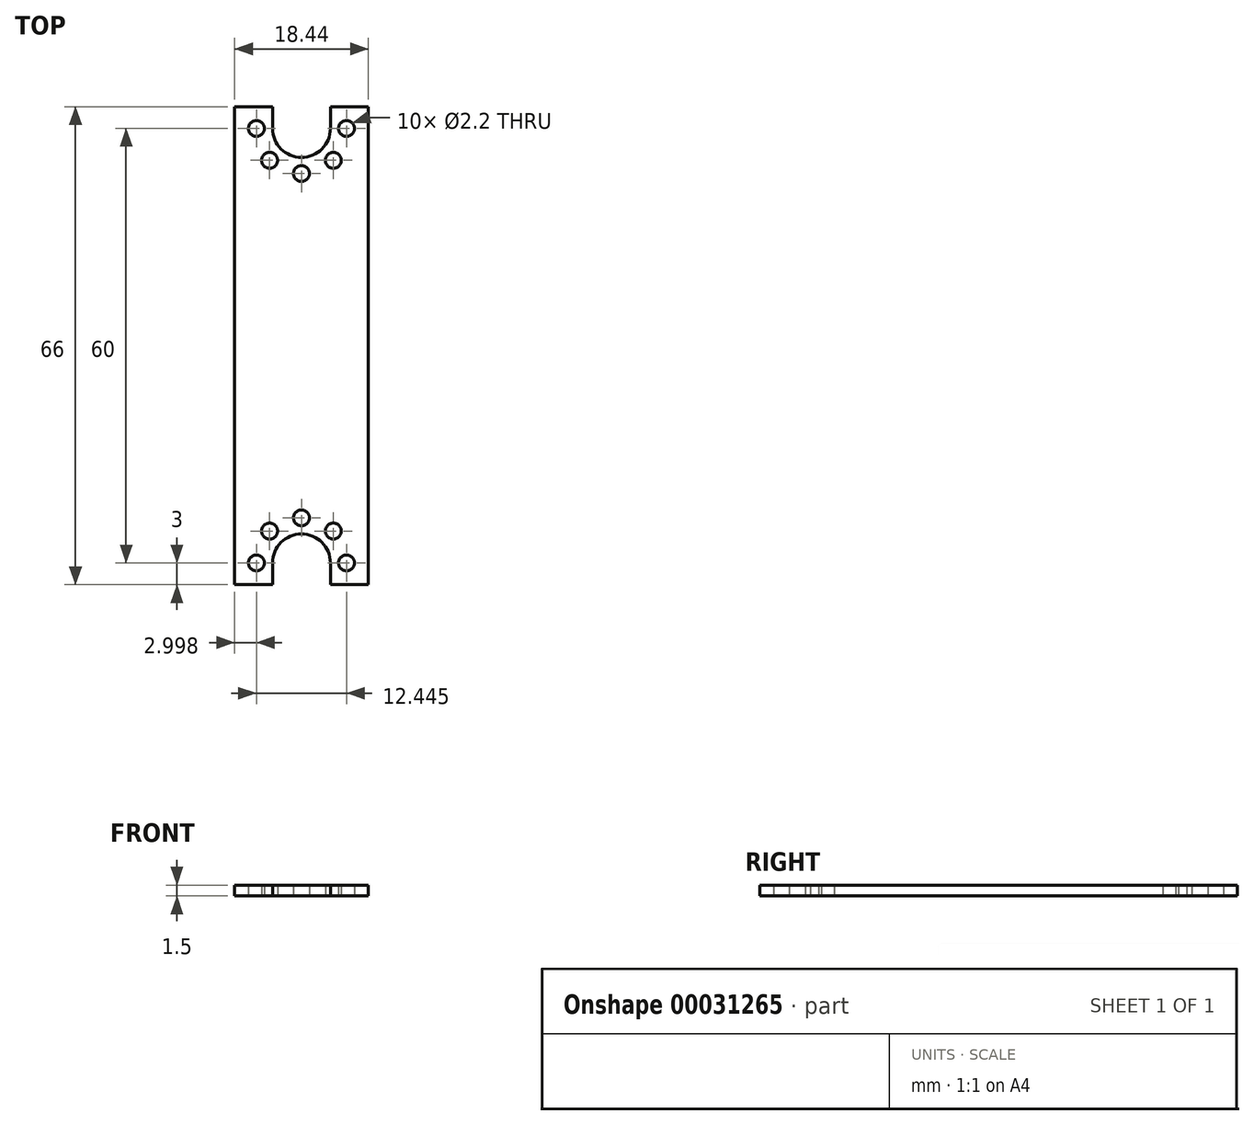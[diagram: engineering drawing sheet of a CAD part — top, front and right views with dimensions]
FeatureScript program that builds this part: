
annotation { "Feature Type Name" : "Feature", "Feature Type Description" : "" }
export const myFeature = defineFeature(function(context is Context, id is Id, definition is map)
    precondition{}
    {
        {
            var Q0;
            Q0=qCreatedBy(makeId("Top.planeOp"),FACE);
            var sketch = newSketch(context, id + "F0", { "sketchPlane" : qUnion([Q0])});
            skLineSegment(sketch, "E0.bottom", {"start": v(-9.22, 33) * mm, "end": v(9.22, 33) * mm});
            skLineSegment(sketch, "E0.top", {"start": v(-9.22, -33) * mm, "end": v(-4, -33) * mm});
            skLineSegment(sketch, "E0.left", {"start": v(-9.22, 33) * mm, "end": v(-9.22, -33) * mm});
            skLineSegment(sketch, "E0.right", {"start": v(9.22, 33) * mm, "end": v(9.22, 27.78) * mm});
            skPoint(sketch, "E0.middle", {"position": v(0, 0) * mm});
            skArc(sketch, "E1", {"start": v(6.22, 27.78) * mm, "mid": v(2.22, 23.78) * mm, "end": v(6.22, 19.78) * mm});
            skArc(sketch, "E2", {"start": v(4, -30) * mm, "mid": v(0, -26) * mm, "end": v(-4, -30) * mm});
            skLineSegment(sketch, "E3.bottom", {"start": v(1.82, 28.18) * mm, "end": v(10.62, 28.18) * mm, "construction": true});
            skLineSegment(sketch, "E3.top", {"start": v(1.82, 19.38) * mm, "end": v(10.62, 19.38) * mm, "construction": true});
            skLineSegment(sketch, "E3.left", {"start": v(1.82, 28.18) * mm, "end": v(1.82, 19.38) * mm, "construction": true});
            skLineSegment(sketch, "E3.right", {"start": v(10.62, 28.18) * mm, "end": v(10.62, 19.38) * mm, "construction": true});
            skCircle(sketch, "E4", {"center": v(1.82, 28.18) * mm, "radius": 1.1 * mm});
            skCircle(sketch, "E5.1.0", {"center": v(0, 23.78) * mm, "radius": 1.1 * mm});
            skCircle(sketch, "E5.2.0", {"center": v(1.82, 19.38) * mm, "radius": 1.1 * mm});
            skCircle(sketch, "E5.3.0", {"center": v(6.22, 17.55) * mm, "radius": 1.1 * mm});
            skCircle(sketch, "E5.7.0", {"center": v(6.22, 30) * mm, "radius": 1.1 * mm});
            skLineSegment(sketch, "E6.bottom", {"start": v(-4.4, -25.6) * mm, "end": v(4.4, -25.6) * mm, "construction": true});
            skLineSegment(sketch, "E6.top", {"start": v(-4.4, -34.4) * mm, "end": v(4.4, -34.4) * mm, "construction": true});
            skLineSegment(sketch, "E6.left", {"start": v(-4.4, -25.6) * mm, "end": v(-4.4, -34.4) * mm, "construction": true});
            skLineSegment(sketch, "E6.right", {"start": v(4.4, -25.6) * mm, "end": v(4.4, -34.4) * mm, "construction": true});
            skCircle(sketch, "E7", {"center": v(4.4, -25.6) * mm, "radius": 1.1 * mm});
            skCircle(sketch, "E8.1.0", {"center": v(0, -23.78) * mm, "radius": 1.1 * mm});
            skCircle(sketch, "E8.2.0", {"center": v(-4.4, -25.6) * mm, "radius": 1.1 * mm});
            skCircle(sketch, "E8.3.0", {"center": v(-6.22, -30) * mm, "radius": 1.1 * mm});
            skCircle(sketch, "E8.7.0", {"center": v(6.22, -30) * mm, "radius": 1.1 * mm});
            skLineSegment(sketch, "E9", {"start": v(6.22, 27.78) * mm, "end": v(9.22, 27.78) * mm});
            skLineSegment(sketch, "E10", {"start": v(6.22, 19.78) * mm, "end": v(9.22, 19.78) * mm});
            skLineSegment(sketch, "E11.trimOffspring", {"start": v(9.22, 19.78) * mm, "end": v(9.22, -33) * mm});
            skLineSegment(sketch, "E12", {"start": v(4, -30) * mm, "end": v(4, -33) * mm});
            skLineSegment(sketch, "E13", {"start": v(-4, -30) * mm, "end": v(-4, -33) * mm});
            skLineSegment(sketch, "E14.trimOffspring", {"start": v(4, -33) * mm, "end": v(9.22, -33) * mm});
            skSolve(sketch);
        }
        {
            var Q0;
            Q0=qSketchRegion(id+"F0",true);
            extrude(context, id + "F1", {"entities" : qUnion([Q0]), "depth" : 1.5 * mm});
        }
        {
            var Q0;
            Q0=makeQuery(id+"F1.opExtrude","CAP_FACE",FACE,{"disambiguationData":[OSD([sQuery(id+"F0.wireOp",EDGE,"E0.bottom"),sQuery(id+"F0.wireOp",EDGE,"E0.top"),sQuery(id+"F0.wireOp",EDGE,"E0.left"),sQuery(id+"F0.wireOp",EDGE,"E0.right"),sQuery(id+"F0.wireOp",EDGE,"E1"),sQuery(id+"F0.wireOp",EDGE,"E2"),sQuery(id+"F0.wireOp",EDGE,"E4"),sQuery(id+"F0.wireOp",EDGE,"E5.1.0"),sQuery(id+"F0.wireOp",EDGE,"E5.2.0"),sQuery(id+"F0.wireOp",EDGE,"E5.3.0"),sQuery(id+"F0.wireOp",EDGE,"E5.7.0"),sQuery(id+"F0.wireOp",EDGE,"E7"),sQuery(id+"F0.wireOp",EDGE,"E8.1.0"),sQuery(id+"F0.wireOp",EDGE,"E8.2.0"),sQuery(id+"F0.wireOp",EDGE,"E8.3.0"),sQuery(id+"F0.wireOp",EDGE,"E8.7.0"),sQuery(id+"F0.wireOp",EDGE,"E9"),sQuery(id+"F0.wireOp",EDGE,"E10"),sQuery(id+"F0.wireOp",EDGE,"E11.trimOffspring"),sQuery(id+"F0.wireOp",EDGE,"E12"),sQuery(id+"F0.wireOp",EDGE,"E13"),sQuery(id+"F0.wireOp",EDGE,"E14.trimOffspring")])],"isStart":false});
            var sketch = newSketch(context, id + "F2", { "sketchPlane" : qUnion([Q0])});
            skLineSegment(sketch, "E15.bottom", {"start": v(9.22, 0) * mm, "end": v(-9.22, 0) * mm});
            skLineSegment(sketch, "E15.top", {"start": v(9.22, 33) * mm, "end": v(-9.22, 33) * mm});
            skLineSegment(sketch, "E15.left", {"start": v(9.22, 0) * mm, "end": v(9.22, 33) * mm});
            skLineSegment(sketch, "E15.right", {"start": v(-9.22, 0) * mm, "end": v(-9.22, 33) * mm});
            skSolve(sketch);
        }
        {
            var Q0;
            {var subQ0=sQuery(id+"F2.wireOp",EDGE,"E15.bottom");Q0=makeQuery(id+"F2.imprint","IMPRINT",FACE,{"disambiguationData":[TD([[makeQuery(id+"F2.imprint","IMPRINT",EDGE,{"derivedFrom":subQ0}),-1.0]])]});}
            extrude(context, id + "F3", {"entities" : qUnion([Q0]), "operationType" : NewBodyOperationType.REMOVE, "endBound" : BoundingType.UP_TO_NEXT, "oppositeDirection" : true, "depth" : 25 * mm});
        }
        {
            var Q0;
            Q0=makeQuery(id+"F1.opExtrude","SWEPT_BODY",BODY,{"disambiguationData":[OSD([sQuery(id+"F0.wireOp",EDGE,"E0.bottom"),sQuery(id+"F0.wireOp",EDGE,"E0.top"),sQuery(id+"F0.wireOp",EDGE,"E0.left"),sQuery(id+"F0.wireOp",EDGE,"E0.right"),sQuery(id+"F0.wireOp",EDGE,"E1"),sQuery(id+"F0.wireOp",EDGE,"E2"),sQuery(id+"F0.wireOp",EDGE,"E4"),sQuery(id+"F0.wireOp",EDGE,"E5.1.0"),sQuery(id+"F0.wireOp",EDGE,"E5.2.0"),sQuery(id+"F0.wireOp",EDGE,"E5.3.0"),sQuery(id+"F0.wireOp",EDGE,"E5.7.0"),sQuery(id+"F0.wireOp",EDGE,"E7"),sQuery(id+"F0.wireOp",EDGE,"E8.1.0"),sQuery(id+"F0.wireOp",EDGE,"E8.2.0"),sQuery(id+"F0.wireOp",EDGE,"E8.3.0"),sQuery(id+"F0.wireOp",EDGE,"E8.7.0"),sQuery(id+"F0.wireOp",EDGE,"E9"),sQuery(id+"F0.wireOp",EDGE,"E10"),sQuery(id+"F0.wireOp",EDGE,"E11.trimOffspring"),sQuery(id+"F0.wireOp",EDGE,"E12"),sQuery(id+"F0.wireOp",EDGE,"E13"),sQuery(id+"F0.wireOp",EDGE,"E14.trimOffspring")])]});
            var Q1;
            Q1=qCreatedBy(makeId("Front.planeOp"),FACE);
            mirror(context, id + "F4", {"operationType" : NewBodyOperationType.ADD, "entities" : qUnion([Q0]), "mirrorPlane" : qUnion([Q1])});
        }
    });
